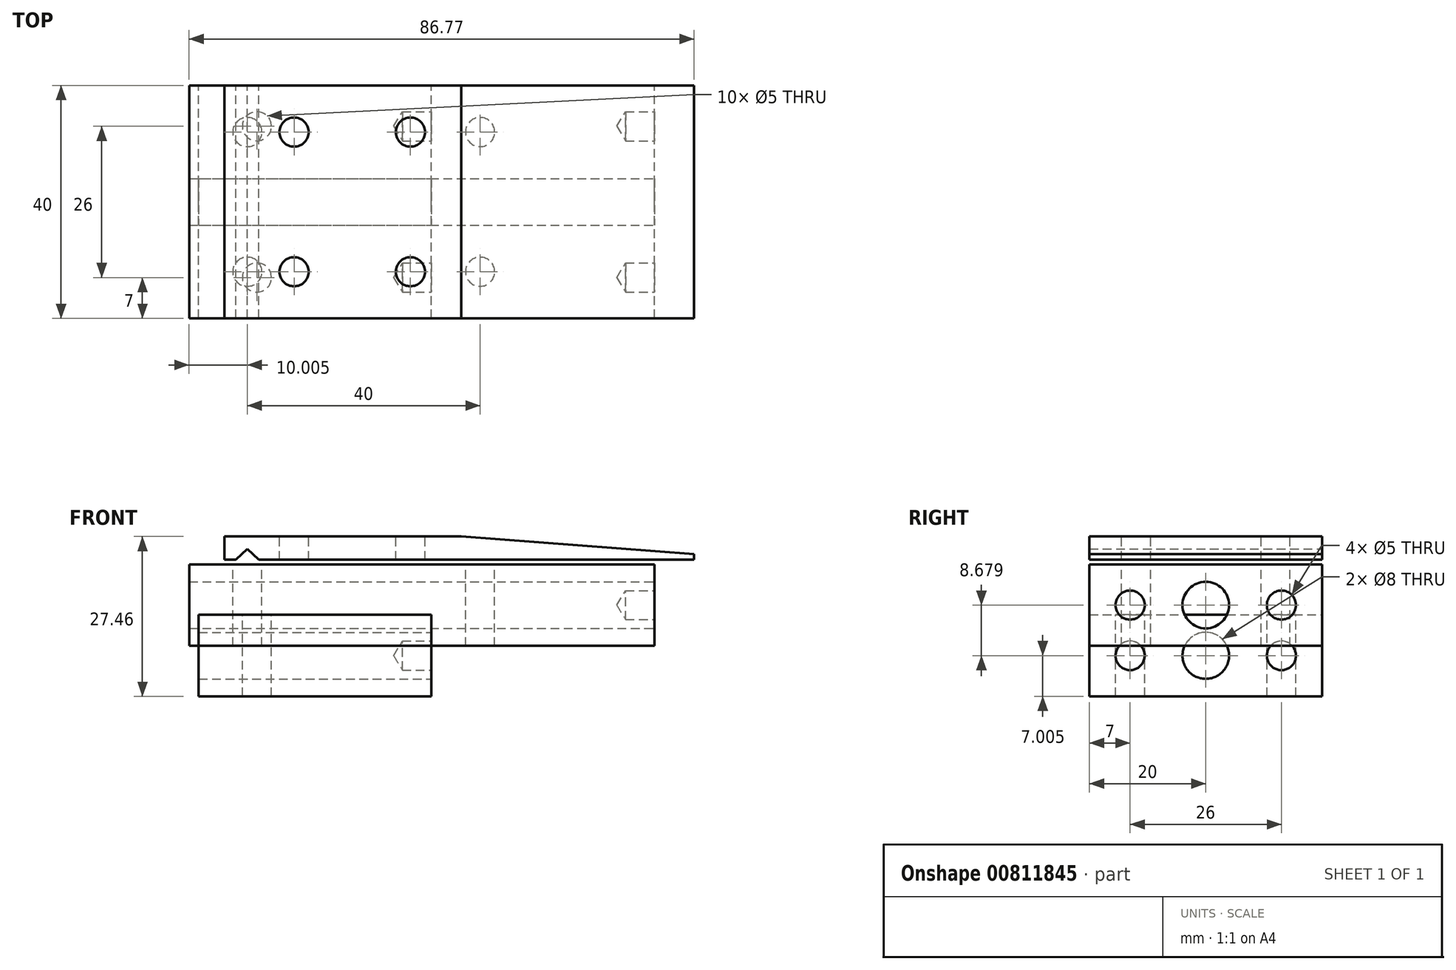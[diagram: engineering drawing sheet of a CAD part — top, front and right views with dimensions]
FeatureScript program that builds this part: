
annotation { "Feature Type Name" : "Feature", "Feature Type Description" : "" }
export const myFeature = defineFeature(function(context is Context, id is Id, definition is map)
    precondition{}
    {
        {
            var Q0;
            Q0=qCreatedBy(makeId("Front.planeOp"),FACE);
            var sketch = newSketch(context, id + "F0", { "sketchPlane" : qUnion([Q0])});
            skLineSegment(sketch, "E0.bottom", {"start": v(-36.5, 13.31) * mm, "end": v(4.24, 13.31) * mm});
            skLineSegment(sketch, "E0.left", {"start": v(-36.5, 13.31) * mm, "end": v(-36.5, 9.31) * mm});
            skLineSegment(sketch, "E0.right", {"start": v(4.24, 13.31) * mm, "end": v(4.24, 9.31) * mm});
            skLineSegment(sketch, "E1", {"start": v(4.24, 9.31) * mm, "end": v(44.24, 9.31) * mm});
            skLineSegment(sketch, "E2", {"start": v(44.24, 9.31) * mm, "end": v(44.24, 10.31) * mm});
            skLineSegment(sketch, "E3", {"start": v(44.24, 10.31) * mm, "end": v(4.24, 13.31) * mm});
            skLineSegment(sketch, "E4", {"start": v(-34.5, 9.31) * mm, "end": v(-32.55, 11.15) * mm});
            skLineSegment(sketch, "E5", {"start": v(-32.55, 11.15) * mm, "end": v(-30.58, 9.31) * mm});
            skLineSegment(sketch, "E6", {"start": v(-36.5, 9.31) * mm, "end": v(-34.5, 9.31) * mm});
            skLineSegment(sketch, "E7", {"start": v(-30.58, 9.31) * mm, "end": v(4.24, 9.31) * mm});
            skSolve(sketch);
        }
        {
            var Q0;
            Q0 = qSketchRegion(id + "F0", true);
            extrude(context, id + "F1", {"entities" : qUnion([Q0]), "endBound" : BoundingType.SYMMETRIC, "depth" : 40 * mm, "offsetDistance" : 25 * mm});
        }
        {
            var Q0;
            Q0=makeQuery(id+"F1.opExtrude","SWEPT_FACE",FACE,{"disambiguationData":[OSD([sQuery(id+"F0.wireOp",EDGE,"E0.bottom")])]});
            var sketch = newSketch(context, id + "F2", { "sketchPlane" : qUnion([Q0])});
            skLineSegment(sketch, "E8.bottom", {"start": v(-24.5, 12) * mm, "end": v(-4.5, 12) * mm});
            skLineSegment(sketch, "E8.top", {"start": v(-24.5, -12) * mm, "end": v(-4.5, -12) * mm});
            skLineSegment(sketch, "E8.left", {"start": v(-24.5, 12) * mm, "end": v(-24.5, -12) * mm});
            skLineSegment(sketch, "E8.right", {"start": v(-4.5, 12) * mm, "end": v(-4.5, -12) * mm});
            skSolve(sketch);
        }
        {
            var Q0;
            Q0=sQuery(id+"F2.wireOp",VERTEX,"E8.bottom.start");
            var Q1;
            Q1=sQuery(id+"F2.wireOp",VERTEX,"E8.bottom.end");
            var Q2;
            Q2=sQuery(id+"F2.wireOp",VERTEX,"E8.top.start");
            var Q3;
            Q3=sQuery(id+"F2.wireOp",VERTEX,"E8.top.end");
            var Q4;
            Q4=makeQuery(id+"F1.opExtrude","SWEPT_BODY",BODY,{"disambiguationData":[OSD([sQuery(id+"F0.wireOp",EDGE,"E0.bottom"),sQuery(id+"F0.wireOp",EDGE,"E0.top"),sQuery(id+"F0.wireOp",EDGE,"E0.left"),sQuery(id+"F0.wireOp",EDGE,"E1"),sQuery(id+"F0.wireOp",EDGE,"E2"),sQuery(id+"F0.wireOp",EDGE,"E3")])]});
            hole(context, id + "F3", {"style" : HoleStyle.SIMPLE, "endStyle" : HoleEndStyle.THROUGH, "holeDiameter" : 5 * mm, "majorDiameter" : 5 * mm, "isTappedThrough" : true, "tappedDepth" : 12.7 * mm, "tapClearance" : 3, "locations" : qUnion([Q0, Q1, Q2, Q3]), "scope" : qUnion([Q4])});
        }
        {
            var Q0;
            Q0=qCreatedBy(makeId("Front.planeOp"),FACE);
            var sketch = newSketch(context, id + "F4", { "sketchPlane" : qUnion([Q0])});
            skLineSegment(sketch, "E9.bottom", {"start": v(-40.88, -0.15) * mm, "end": v(-0.88, -0.15) * mm});
            skLineSegment(sketch, "E9.top", {"start": v(-40.88, -14.15) * mm, "end": v(-0.88, -14.15) * mm});
            skLineSegment(sketch, "E9.left", {"start": v(-40.88, -0.15) * mm, "end": v(-40.88, -14.15) * mm});
            skLineSegment(sketch, "E9.right", {"start": v(-0.88, -0.15) * mm, "end": v(-0.88, -14.15) * mm});
            skSolve(sketch);
        }
        {
            var Q0;
            Q0=makeQuery(id+"F4.imprint","IMPRINT",FACE,{"disambiguationData":[TD([[makeQuery(id+"F4.imprint","IMPRINT",EDGE,{"derivedFrom":sQuery(id+"F4.wireOp",EDGE,"E9.bottom")}),-1.0]])]});
            extrude(context, id + "F5", {"entities" : qUnion([Q0]), "endBound" : BoundingType.SYMMETRIC, "depth" : 40 * mm, "offsetDistance" : 25 * mm});
        }
        {
            var Q0;
            Q0=makeQuery(id+"F5.opExtrude","SWEPT_FACE",FACE,{"disambiguationData":[OSD([sQuery(id+"F4.wireOp",EDGE,"E9.bottom")])]});
            var sketch = newSketch(context, id + "F6", { "sketchPlane" : qUnion([Q0])});
            skLineSegment(sketch, "E10", {"start": v(-30.88, 13) * mm, "end": v(-30.88, -13) * mm});
            skSolve(sketch);
        }
        {
            var Q0;
            Q0=sQuery(id+"F6.wireOp",VERTEX,"E10.start");
            var Q1;
            Q1=sQuery(id+"F6.wireOp",VERTEX,"E10.end");
            var Q2;
            Q2=makeQuery(id+"F5.opExtrude","SWEPT_BODY",BODY,{"disambiguationData":[OSD([sQuery(id+"F4.wireOp",EDGE,"E9.bottom"),sQuery(id+"F4.wireOp",EDGE,"E9.top"),sQuery(id+"F4.wireOp",EDGE,"E9.left"),sQuery(id+"F4.wireOp",EDGE,"E9.right")])]});
            hole(context, id + "F7", {"style" : HoleStyle.SIMPLE, "endStyle" : HoleEndStyle.THROUGH, "holeDiameter" : 5 * mm, "majorDiameter" : 5 * mm, "isTappedThrough" : true, "tappedDepth" : 12.7 * mm, "tapClearance" : 3, "locations" : qUnion([Q0, Q1]), "scope" : qUnion([Q2])});
        }
        {
            var Q0;
            Q0=makeQuery(id+"F5.opExtrude","SWEPT_FACE",FACE,{"disambiguationData":[OSD([sQuery(id+"F4.wireOp",EDGE,"E9.right")])]});
            var sketch = newSketch(context, id + "F8", { "sketchPlane" : qUnion([Q0])});
            skPoint(sketch, "E11", {"position": v(0, -7.15) * mm});
            skSolve(sketch);
        }
        {
            var Q0;
            Q0=sQuery(id+"F8.wireOp",VERTEX,"E11");
            var Q1;
            Q1=makeQuery(id+"F5.opExtrude","SWEPT_BODY",BODY,{"disambiguationData":[OSD([sQuery(id+"F4.wireOp",EDGE,"E9.bottom"),sQuery(id+"F4.wireOp",EDGE,"E9.top"),sQuery(id+"F4.wireOp",EDGE,"E9.left"),sQuery(id+"F4.wireOp",EDGE,"E9.right")])]});
            hole(context, id + "F9", {"style" : HoleStyle.SIMPLE, "endStyle" : HoleEndStyle.THROUGH, "holeDiameter" : 8 * mm, "majorDiameter" : 5 * mm, "isTappedThrough" : true, "tappedDepth" : 12.7 * mm, "tapClearance" : 3, "locations" : qUnion([Q0]), "scope" : qUnion([Q1])});
        }
        {
            var Q0;
            Q0=qCreatedBy(makeId("Front.planeOp"),FACE);
            var sketch = newSketch(context, id + "F10", { "sketchPlane" : qUnion([Q0])});
            skLineSegment(sketch, "E12.bottom", {"start": v(-42.53, 8.53) * mm, "end": v(37.47, 8.53) * mm});
            skLineSegment(sketch, "E12.top", {"start": v(-42.53, -5.47) * mm, "end": v(37.47, -5.47) * mm});
            skLineSegment(sketch, "E12.left", {"start": v(-42.53, 8.53) * mm, "end": v(-42.53, -5.47) * mm});
            skLineSegment(sketch, "E12.right", {"start": v(37.47, 8.53) * mm, "end": v(37.47, -5.47) * mm});
            skSolve(sketch);
        }
        {
            var Q0;
            Q0=makeQuery(id+"F10.imprint","IMPRINT",FACE,{"disambiguationData":[TD([[makeQuery(id+"F10.imprint","IMPRINT",EDGE,{"derivedFrom":sQuery(id+"F10.wireOp",EDGE,"E12.bottom")}),-1.0]])]});
            extrude(context, id + "F11", {"entities" : qUnion([Q0]), "endBound" : BoundingType.SYMMETRIC, "depth" : 40 * mm, "offsetDistance" : 25 * mm});
        }
        {
            var Q0;
            Q0=makeQuery(id+"F11.opExtrude","SWEPT_FACE",FACE,{"disambiguationData":[OSD([sQuery(id+"F10.wireOp",EDGE,"E12.bottom")])]});
            var sketch = newSketch(context, id + "F12", { "sketchPlane" : qUnion([Q0])});
            skLineSegment(sketch, "E13.bottom", {"start": v(-32.53, 12) * mm, "end": v(7.47, 12) * mm});
            skLineSegment(sketch, "E13.top", {"start": v(-32.53, -12) * mm, "end": v(7.47, -12) * mm});
            skLineSegment(sketch, "E13.left", {"start": v(-32.53, 12) * mm, "end": v(-32.53, -12) * mm});
            skLineSegment(sketch, "E13.right", {"start": v(7.47, 12) * mm, "end": v(7.47, -12) * mm});
            skSolve(sketch);
        }
        {
            var Q0;
            Q0=sQuery(id+"F12.wireOp",VERTEX,"E13.bottom.start");
            var Q1;
            Q1=sQuery(id+"F12.wireOp",VERTEX,"E13.top.start");
            var Q2;
            Q2=sQuery(id+"F12.wireOp",VERTEX,"E13.top.end");
            var Q3;
            Q3=sQuery(id+"F12.wireOp",VERTEX,"E13.bottom.end");
            var Q4;
            Q4=makeQuery(id+"F11.opExtrude","SWEPT_BODY",BODY,{"disambiguationData":[OSD([sQuery(id+"F10.wireOp",EDGE,"E12.bottom"),sQuery(id+"F10.wireOp",EDGE,"E12.top"),sQuery(id+"F10.wireOp",EDGE,"E12.left"),sQuery(id+"F10.wireOp",EDGE,"E12.right")])]});
            hole(context, id + "F13", {"style" : HoleStyle.SIMPLE, "endStyle" : HoleEndStyle.THROUGH, "holeDiameter" : 5 * mm, "majorDiameter" : 5 * mm, "isTappedThrough" : true, "tappedDepth" : 12.7 * mm, "tapClearance" : 3, "locations" : qUnion([Q0, Q1, Q2, Q3]), "scope" : qUnion([Q4])});
        }
        {
            var Q0;
            Q0=makeQuery(id+"F11.opExtrude","SWEPT_FACE",FACE,{"disambiguationData":[OSD([sQuery(id+"F10.wireOp",EDGE,"E12.right")])]});
            var sketch = newSketch(context, id + "F14", { "sketchPlane" : qUnion([Q0])});
            skPoint(sketch, "E14", {"position": v(0, 1.53) * mm});
            skSolve(sketch);
        }
        {
            var Q0;
            Q0=sQuery(id+"F14.wireOp",VERTEX,"E14");
            var Q1;
            Q1=makeQuery(id+"F11.opExtrude","SWEPT_BODY",BODY,{"disambiguationData":[OSD([sQuery(id+"F10.wireOp",EDGE,"E12.bottom"),sQuery(id+"F10.wireOp",EDGE,"E12.top"),sQuery(id+"F10.wireOp",EDGE,"E12.left"),sQuery(id+"F10.wireOp",EDGE,"E12.right")])]});
            hole(context, id + "F15", {"style" : HoleStyle.SIMPLE, "endStyle" : HoleEndStyle.THROUGH, "holeDiameter" : 8 * mm, "majorDiameter" : 5 * mm, "isTappedThrough" : true, "tappedDepth" : 12.7 * mm, "tapClearance" : 3, "locations" : qUnion([Q0]), "scope" : qUnion([Q1])});
        }
        {
            var Q0;
            Q0=makeQuery(id+"F5.opExtrude","SWEPT_FACE",FACE,{"disambiguationData":[OSD([sQuery(id+"F4.wireOp",EDGE,"E9.right")])]});
            var sketch = newSketch(context, id + "F16", { "sketchPlane" : qUnion([Q0])});
            skPoint(sketch, "E15", {"position": v(-13, -7.15) * mm});
            skPoint(sketch, "E16", {"position": v(13, -7.15) * mm});
            skSolve(sketch);
        }
        {
            var Q0;
            Q0=sQuery(id+"F16.wireOp",VERTEX,"E15");
            var Q1;
            Q1=sQuery(id+"F16.wireOp",VERTEX,"E16");
            var Q2;
            Q2=makeQuery(id+"F5.opExtrude","SWEPT_BODY",BODY,{"disambiguationData":[OSD([sQuery(id+"F4.wireOp",EDGE,"E9.bottom"),sQuery(id+"F4.wireOp",EDGE,"E9.top"),sQuery(id+"F4.wireOp",EDGE,"E9.left"),sQuery(id+"F4.wireOp",EDGE,"E9.right")])]});
            hole(context, id + "F17", {"style" : HoleStyle.SIMPLE, "endStyle" : HoleEndStyle.BLIND, "holeDiameter" : 5 * mm, "majorDiameter" : 5 * mm, "holeDepth" : 5 * mm, "isTappedThrough" : true, "tappedDepth" : 12.7 * mm, "tapClearance" : 3, "locations" : qUnion([Q0, Q1]), "scope" : qUnion([Q2])});
        }
        {
            var Q0;
            Q0=makeQuery(id+"F11.opExtrude","SWEPT_FACE",FACE,{"disambiguationData":[OSD([sQuery(id+"F10.wireOp",EDGE,"E12.right")])]});
            var sketch = newSketch(context, id + "F18", { "sketchPlane" : qUnion([Q0])});
            skPoint(sketch, "E17", {"position": v(-13, 1.53) * mm});
            skPoint(sketch, "E18", {"position": v(13, 1.53) * mm});
            skSolve(sketch);
        }
        {
            var Q0;
            Q0=sQuery(id+"F18.wireOp",VERTEX,"E17");
            var Q1;
            Q1=sQuery(id+"F18.wireOp",VERTEX,"E18");
            var Q2;
            Q2=makeQuery(id+"F11.opExtrude","SWEPT_BODY",BODY,{"disambiguationData":[OSD([sQuery(id+"F10.wireOp",EDGE,"E12.bottom"),sQuery(id+"F10.wireOp",EDGE,"E12.top"),sQuery(id+"F10.wireOp",EDGE,"E12.left"),sQuery(id+"F10.wireOp",EDGE,"E12.right")])]});
            hole(context, id + "F19", {"style" : HoleStyle.SIMPLE, "endStyle" : HoleEndStyle.BLIND, "holeDiameter" : 5 * mm, "majorDiameter" : 5 * mm, "holeDepth" : 5 * mm, "isTappedThrough" : true, "tappedDepth" : 12.7 * mm, "tapClearance" : 3, "locations" : qUnion([Q0, Q1]), "scope" : qUnion([Q2])});
        }
    });
